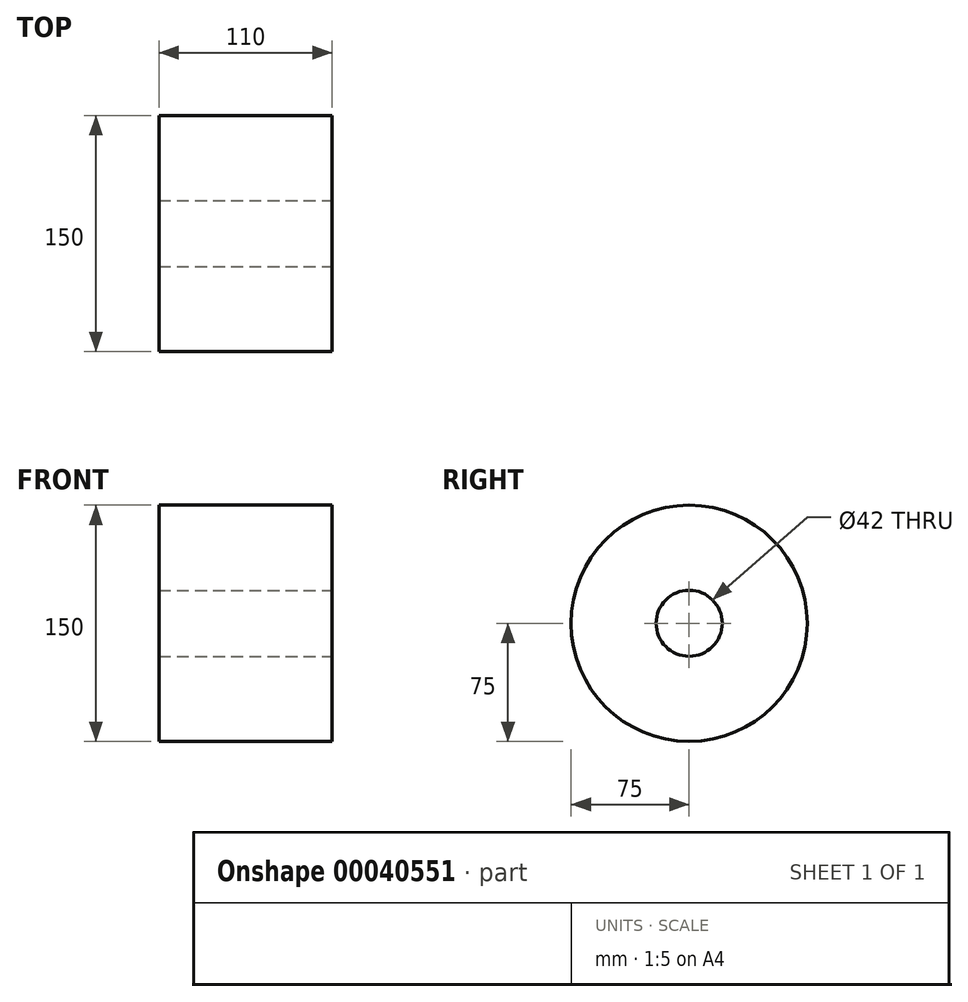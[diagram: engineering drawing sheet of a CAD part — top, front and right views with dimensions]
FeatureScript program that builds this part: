
annotation { "Feature Type Name" : "Feature", "Feature Type Description" : "" }
export const myFeature = defineFeature(function(context is Context, id is Id, definition is map)
    precondition{}
    {
        {
            var Q0;
            Q0=qCreatedBy(makeId("Right.planeOp"),FACE);
            var sketch = newSketch(context, id + "F0", { "sketchPlane" : qUnion([Q0])});
            skCircle(sketch, "E0", {"center": v(0, 0) * mm, "radius": 75 * mm});
            skSolve(sketch);
        }
        {
            var Q0;
            Q0=makeQuery(id+"F0.imprint","IMPRINT",FACE,{"disambiguationData":[TD([[makeQuery(id+"F0.imprint","IMPRINT",EDGE,{"derivedFrom":sQuery(id+"F0.wireOp",EDGE,"E0")}),1.0]])]});
            extrude(context, id + "F1", {"entities" : qUnion([Q0]), "depth" : 110 * mm});
        }
        {
            var Q0;
            Q0=makeQuery(id+"F1.opExtrude","CAP_FACE",FACE,{"disambiguationData":[OSD([sQuery(id+"F0.wireOp",EDGE,"E0")])],"isStart":false});
            var sketch = newSketch(context, id + "F2", { "sketchPlane" : qUnion([Q0])});
            skCircle(sketch, "E1", {"center": v(0, 0) * mm, "radius": 21 * mm});
            skSolve(sketch);
        }
        {
            var Q0;
            Q0=makeQuery(id+"F2.imprint","IMPRINT",FACE,{"disambiguationData":[TD([[makeQuery(id+"F2.imprint","IMPRINT",EDGE,{"derivedFrom":sQuery(id+"F2.wireOp",EDGE,"E1")}),1.0]])]});
            extrude(context, id + "F3", {"entities" : qUnion([Q0]), "operationType" : NewBodyOperationType.REMOVE, "endBound" : BoundingType.THROUGH_ALL, "oppositeDirection" : true, "depth" : 25 * mm});
        }
    });
